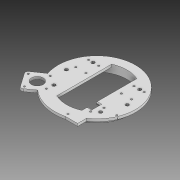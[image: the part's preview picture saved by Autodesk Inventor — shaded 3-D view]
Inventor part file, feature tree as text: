
AUTODESK INVENTOR PART (.ipt)
format: ipt  version: 2020 (Build 240168000, 168)  size: 633,856 bytes
history: native  units: mm
features: extrude x20, sketch x18, revolve x1, plane x1, fillet x1, chamfer x1, projected_geometry x1
ambient origin geometry x8: Origin, YZ Plane, XZ Plane, XY Plane, X Axis, Y Axis, Z Axis, Center Point
bodies: Solid1 (feature_tree)
feature tree (43):
  revolve  "Revolution1"  [1 undecoded]
  extrude  "Extrusion1"  Depth=3.0mm
  extrude  "Extrusion2"  TaperAngle=90.0deg  [1 undecoded]
  extrude  "Extrusion3"  Depth=5.0mm
  sketch  "Sketch5"  dims[d8=76.0mm d9=49.5mm]
  extrude  "Extrusion4"  Depth=49.5mm
  extrude  "Extrusion5"  Depth=26.0mm
  extrude  "Extrusion6"  Depth=25.0mm
  plane  "Work Plane1"
  extrude  "Extrusion7"  Depth=3.5mm
  extrude  "Extrusion8"  Depth=60.0mm
  extrude  "Extrusion9"  Depth=5.0mm TaperAngle=0.0deg
  extrude  "Extrusion10"  Depth=31.0mm
  extrude  "Extrusion11"  Depth=10.0mm TaperAngle=0.0deg
  fillet  "Fillet1"  Radius=3.5mm
  extrude  "Extrusion12"  Depth=9.599311mm
  extrude  "Extrusion13"  Depth=6.0mm
  extrude  "Extrusion14"  Depth=5.0mm
  sketch  "Sketch15"  dims[d32=0.0mm d33=0.0mm d34=6.0mm]
  extrude  "Extrusion15"  [1 undecoded]
  extrude  "Extrusion16"  Depth=23.0mm
  extrude  "Extrusion17"  Depth=10.0mm
  extrude  "Extrusion18"  Depth=10.0mm
  extrude  "Extrusion19"  Depth=10.0mm
  extrude  "Extrusion20"  Depth=10.0mm
  chamfer  "Chamfer1"  Distance=4.0mm
  sketch  "Sketch1"  dims[d0=63.4mm d1=4.0mm]
  sketch  "Sketch2"  dims[d2=2.5mm d3=3.0mm]
  sketch  "Sketch3"  dims[d4=5.0mm d5=90.0deg]
  sketch  "Sketch4"  dims[d6=6.0mm d7=5.0mm]
  sketch  "Sketch6"  dims[d10=5.0mm d11=0.0mm d12=26.0mm]
  sketch  "Sketch7"  dims[d14=20.0mm d15=25.0mm]
  sketch  "Sketch8"  dims[d16=20.0mm d17=3.5mm]
  sketch  "Sketch10"  dims[d18=0.0mm d19=0.0mm d20=60.0mm]
  sketch  "Sketch11"  dims[d21=50.0mm d22=5.0mm d23=0.0mm]
  sketch  "Sketch12"  dims[d24=20.6mm d25=31.0mm]
  sketch  "Sketch13"  dims[d26=42.0mm d27=10.0mm d28=0.0mm d29=3.5mm]
  projected_geometry  "Projected Loop1"
  sketch  "Sketch14"  dims[d30=23.0mm d31=9.599311mm]
  sketch  "Sketch16"  dims[d35=3.0mm d36=0.0mm d37=5.0mm]
  sketch  "Sketch17"  dims[d38=84.0mm d39=-14.0mm]
  sketch  "Sketch18"  dims[d40=84.0mm d41=23.0mm]
  sketch  "Sketch19"  dims[d42=3.5mm d43=31.0mm d44=31.0mm d46=40.0mm d47=43.0mm d48=4.0mm d49=0.0mm d50=4.0mm d51=0.0mm d52=20.0mm d53=3.0mm d54=0.0mm d55=3.0mm d56=0.0mm d57=9.0mm d58=12.0mm d59=16.0mm d60=0.0mm d61=0.0mm d62=2.0mm d63=10.0mm d64=0.0mm d65=0.0mm d66=0.0mm d67=5.8mm d68=15.0mm d69=2.5mm d70=0.0mm d71=0.0mm d72=6.981317mm d73=6.981317mm d74=7.0mm d75=9.0mm d76=3.5mm d77=3.0mm d78=0.0mm d79=3.0mm d80=0.0mm d81=5.8mm d82=5.0mm d83=0.0mm d84=81.937476mm d85=28.359504mm d86=107.09mm d87=0.0mm d97=25.5mm d98=6.5mm d99=18.0mm d100=26.5mm d101=7.0mm d102=19.5mm d103=25.0mm d104=3.5mm d105=4.0mm d106=0.0mm d107=5.8mm d108=3.0mm d109=2.5mm d110=0.0mm d111=0.0mm d112=2.5mm d113=2.0mm d114=45.0deg]
note: 3 required parameter values undecoded (feature->parameter linkage not recoverable at this tier; creation-order binding heuristic only, values carry confidence <= 0.55)